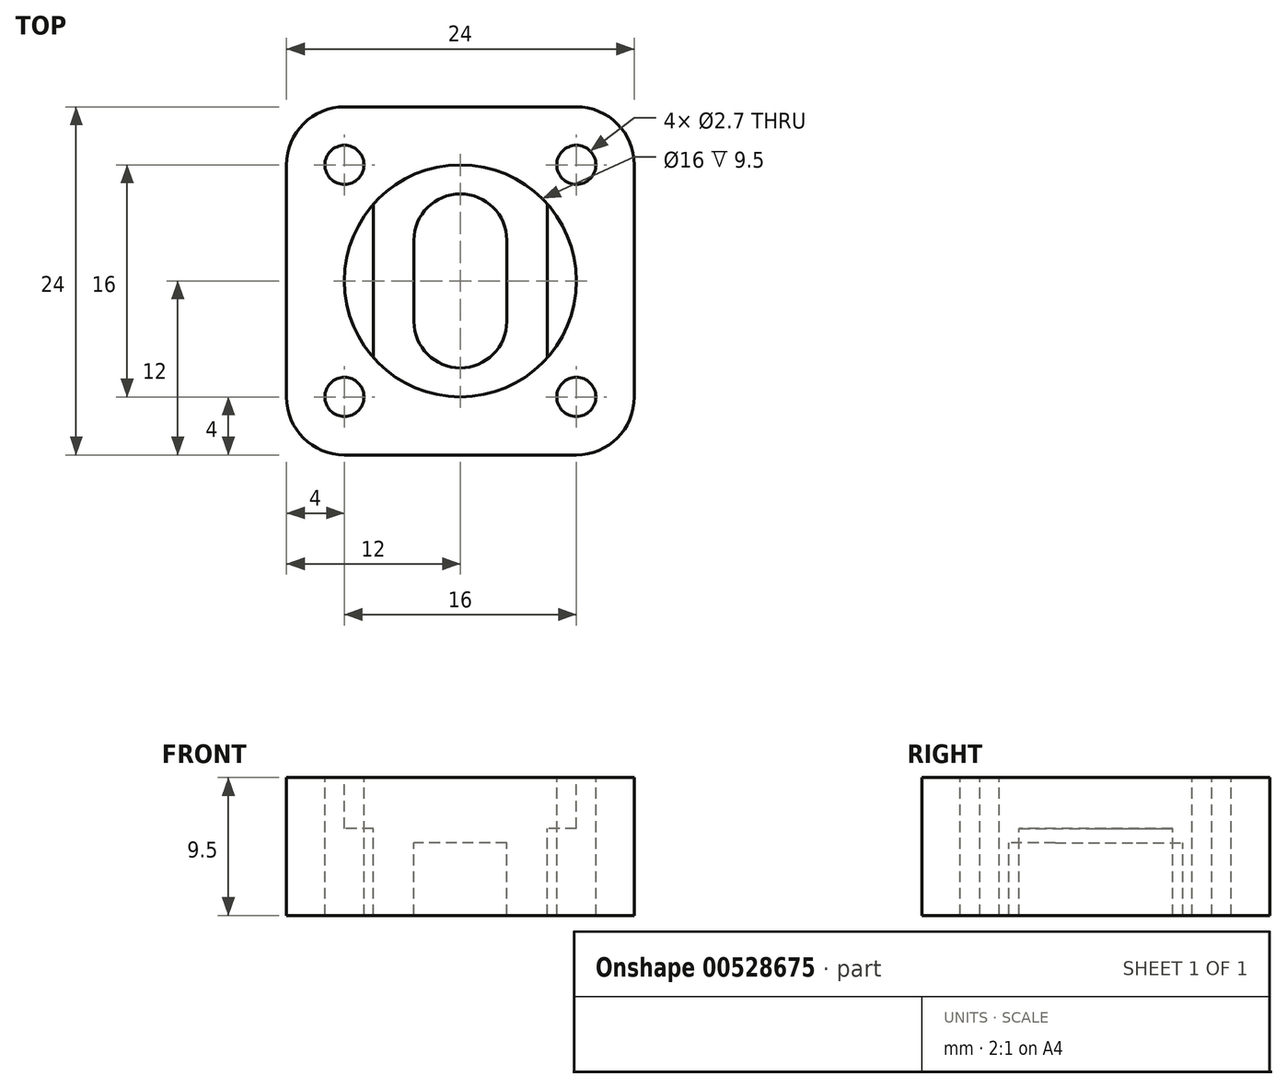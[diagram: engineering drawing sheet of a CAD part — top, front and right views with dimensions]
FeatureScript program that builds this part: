
annotation { "Feature Type Name" : "Feature", "Feature Type Description" : "" }
export const myFeature = defineFeature(function(context is Context, id is Id, definition is map)
    precondition{}
    {
        {
            var Q0;
            Q0=qCreatedBy(makeId("Top.planeOp"),FACE);
            var sketch = newSketch(context, id + "F0", { "sketchPlane" : qUnion([Q0])});
            skLineSegment(sketch, "E0.bottom", {"start": v(0, 0) * mm, "end": v(24, 0) * mm});
            skLineSegment(sketch, "E0.top", {"start": v(0, 24) * mm, "end": v(24, 24) * mm});
            skLineSegment(sketch, "E0.left", {"start": v(0, 0) * mm, "end": v(0, 24) * mm});
            skLineSegment(sketch, "E0.right", {"start": v(24, 0) * mm, "end": v(24, 24) * mm});
            skSolve(sketch);
        }
        {
            var Q0;
            Q0=makeQuery(id+"F0.imprint","IMPRINT",FACE,{"disambiguationData":[TD([[makeQuery(id+"F0.imprint","IMPRINT",EDGE,{"derivedFrom":sQuery(id+"F0.wireOp",EDGE,"E0.bottom")}),1.0]])]});
            extrude(context, id + "F1", {"entities" : qUnion([Q0]), "depth" : 9.5 * mm, "offsetDistance" : 25 * mm});
        }
        {
            var Q0;
            Q0=qCreatedBy(makeId("Top.planeOp"),FACE);
            cPlane(context, id + "F2", {"entities" : qUnion([Q0]), "cplaneType" : CPlaneType.OFFSET, "offset" : 5 * mm, "width" : 150 * mm, "height" : 150 * mm});
        }
        {
            var Q0;
            Q0=qCreatedBy(makeId("Top.planeOp"),FACE);
            cPlane(context, id + "F3", {"entities" : qUnion([Q0]), "cplaneType" : CPlaneType.OFFSET, "offset" : 6 * mm, "width" : 150 * mm, "height" : 150 * mm});
        }
        {
            var Q0;
            Q0=makeQuery(id+"F1.opExtrude","SWEPT_EDGE",EDGE,{"disambiguationData":[OSD([sQuery(id+"F0.wireOp",EDGE,"E0.bottom"),sQuery(id+"F0.wireOp",EDGE,"E0.left")])]});
            var Q1;
            Q1=makeQuery(id+"F1.opExtrude","SWEPT_EDGE",EDGE,{"disambiguationData":[OSD([sQuery(id+"F0.wireOp",EDGE,"E0.bottom"),sQuery(id+"F0.wireOp",EDGE,"E0.right")])]});
            var Q2;
            Q2=makeQuery(id+"F1.opExtrude","SWEPT_EDGE",EDGE,{"disambiguationData":[OSD([sQuery(id+"F0.wireOp",EDGE,"E0.top"),sQuery(id+"F0.wireOp",EDGE,"E0.right")])]});
            var Q3;
            Q3=makeQuery(id+"F1.opExtrude","SWEPT_EDGE",EDGE,{"disambiguationData":[OSD([sQuery(id+"F0.wireOp",EDGE,"E0.top"),sQuery(id+"F0.wireOp",EDGE,"E0.left")])]});
            fillet(context, id + "F4", {"entities" : qUnion([Q0, Q1, Q2, Q3]), "radius" : 4 * mm, "tangentPropagation" : true, "allowEdgeOverflow" : false});
        }
        {
            var Q0;
            Q0=makeQuery(id+"F1.opExtrude","CAP_FACE",FACE,{"disambiguationData":[OSD([sQuery(id+"F0.wireOp",EDGE,"E0.bottom"),sQuery(id+"F0.wireOp",EDGE,"E0.top"),sQuery(id+"F0.wireOp",EDGE,"E0.left"),sQuery(id+"F0.wireOp",EDGE,"E0.right")])],"isStart":false});
            var sketch = newSketch(context, id + "F5", { "sketchPlane" : qUnion([Q0])});
            skCircle(sketch, "E1", {"center": v(4, 4) * mm, "radius": 1.35 * mm});
            skCircle(sketch, "E2.0.1.0", {"center": v(4, 20) * mm, "radius": 1.35 * mm});
            skCircle(sketch, "E2.1.0.0", {"center": v(20, 4) * mm, "radius": 1.35 * mm});
            skCircle(sketch, "E2.1.1.0", {"center": v(20, 20) * mm, "radius": 1.35 * mm});
            skLineSegment(sketch, "E2.direction1", {"start": v(4, 4) * mm, "end": v(20, 4) * mm, "construction": true});
            skLineSegment(sketch, "E2.direction2", {"start": v(4, 4) * mm, "end": v(4, 20) * mm, "construction": true});
            skSolve(sketch);
        }
        {
            var Q0;
            Q0=makeQuery(id+"F5.imprint","IMPRINT",FACE,{"disambiguationData":[TD([[makeQuery(id+"F5.imprint","IMPRINT",EDGE,{"derivedFrom":sQuery(id+"F5.wireOp",EDGE,"E1")}),-1.0]])]});
            var sketch = newSketch(context, id + "F6", { "sketchPlane" : qUnion([Q0])});
            skCircle(sketch, "E3", {"center": v(12, 12) * mm, "radius": 8 * mm});
            skLineSegment(sketch, "E4", {"start": v(12, 12) * mm, "end": v(12, 14.8) * mm, "construction": true});
            skArc(sketch, "E5", {"start": v(8.8, 14.8) * mm, "mid": v(12, 18) * mm, "end": v(15.2, 14.8) * mm});
            skLineSegment(sketch, "E6", {"start": v(12, 12) * mm, "end": v(12, 9.2) * mm, "construction": true});
            skArc(sketch, "E7", {"start": v(8.8, 9.2) * mm, "mid": v(12, 6) * mm, "end": v(15.2, 9.2) * mm});
            skLineSegment(sketch, "E8", {"start": v(8.8, 14.8) * mm, "end": v(8.8, 9.2) * mm});
            skLineSegment(sketch, "E9", {"start": v(15.2, 14.8) * mm, "end": v(15.2, 9.2) * mm});
            skLineSegment(sketch, "E10", {"start": v(12, 12) * mm, "end": v(18, 12) * mm, "construction": true});
            skLineSegment(sketch, "E11", {"start": v(18, 12) * mm, "end": v(18, 17.3) * mm});
            skLineSegment(sketch, "E12.MirrorCS", {"start": v(18, 12) * mm, "end": v(18, 6.7) * mm});
            skLineSegment(sketch, "E13.MirrorCS", {"start": v(6, 12) * mm, "end": v(6, 17.3) * mm});
            skLineSegment(sketch, "E14.MirrorCS", {"start": v(6, 12) * mm, "end": v(6, 6.7) * mm});
            skSolve(sketch);
        }
        {
            var Q0;
            Q0=makeQuery(id+"F6.imprint","IMPRINT",FACE,{"disambiguationData":[TD([[makeQuery(id+"F6.imprint","IMPRINT",EDGE,{"derivedFrom":sQuery(id+"F6.wireOp",EDGE,"E5")}),-1.0]])]});
            extrude(context, id + "F7", {"entities" : qUnion([Q0]), "operationType" : NewBodyOperationType.REMOVE, "endBound" : BoundingType.THROUGH_ALL, "oppositeDirection" : true, "depth" : 12 * mm, "offsetDistance" : 25 * mm});
        }
        {
            var Q0;
            Q0=makeQuery(id+"F6.imprint","IMPRINT",FACE,{"disambiguationData":[TD([[makeQuery(id+"F6.imprint","IMPRINT",EDGE,{"derivedFrom":sQuery(id+"F6.wireOp",EDGE,"E5")}),1.0]])]});
            var Q1;
            Q1=qCreatedBy(id+"F2.planeOp",FACE);
            extrude(context, id + "F8", {"entities" : qUnion([Q0]), "operationType" : NewBodyOperationType.REMOVE, "endBound" : BoundingType.UP_TO_SURFACE, "oppositeDirection" : true, "depth" : 25 * mm, "endBoundEntityFace" : qUnion([Q1]), "offsetDistance" : 25 * mm});
        }
        {
            var Q0;
            {var subQ0=sQuery(id+"F6.wireOp",EDGE,"E13.MirrorCS");Q0=makeQuery(id+"F6.imprint","IMPRINT",FACE,{"disambiguationData":[TD([[makeQuery(id+"F6.imprint","IMPRINT",EDGE,{"derivedFrom":subQ0}),1.0]])]});}
            var Q1;
            {var subQ0=sQuery(id+"F6.wireOp",EDGE,"E11");Q1=makeQuery(id+"F6.imprint","IMPRINT",FACE,{"disambiguationData":[TD([[makeQuery(id+"F6.imprint","IMPRINT",EDGE,{"derivedFrom":subQ0}),-1.0]])]});}
            var Q2;
            Q2=qCreatedBy(id+"F3.planeOp",FACE);
            extrude(context, id + "F9", {"entities" : qUnion([Q0, Q1]), "operationType" : NewBodyOperationType.REMOVE, "endBound" : BoundingType.UP_TO_SURFACE, "oppositeDirection" : true, "depth" : 25 * mm, "endBoundEntityFace" : qUnion([Q2]), "offsetDistance" : 25 * mm});
        }
        {
            var Q0;
            Q0=qSketchRegion(id+"F5",true);
            extrude(context, id + "F10", {"entities" : qUnion([Q0]), "operationType" : NewBodyOperationType.REMOVE, "endBound" : BoundingType.THROUGH_ALL, "oppositeDirection" : true, "depth" : 12 * mm, "offsetDistance" : 25 * mm});
        }
    });
